# Revit family: Lighting-CommercialSector-GEWISS-ELIA-PL-LED_FLUSH_MOUNTING
name_source: partatom
category: Apparecchi per illuminazione
units: mm (PartAtom-declared; Revit-internal decimal feet)

## family parameters
Condiviso = No
Host = Superficie
Punto di calcolo locali = Sì
Quota connettore circolare = Usa diametro
Sorgente d'illuminazione = Sì
Taglio con vuoti quando caricato = No
Tipo di parte = Normale

## types (48) — shared parameters
Angolo inclinazione = -90.00°
Application = Indoor
BORDO = BORDO
Catalogue = LIGHTING
Catalogue Range = ELIA PL
Colour = White
Emetti da lunghezza linea = 610 mm
FORO_CONTROSOFFITTO = 80 mm  [stored 0.262467 ft]
File diagramma fotometrico = GWF1611NN940.IES
Filtro dei colori = 16777215
IDF = 6f387c7b-be92-4833-a933-611e67cbe188
IDT = 4c6a4f10-3f0b-4303-adcc-d543444cbb8d
IP degree = IP20 - IP40
Immagine tipo = ELIA_PL_q.jpg
Installation = Modular flush mounting
Insulation class = II
LED Life time (L80B50) = L80 B50 (Tq25°) = 50.000h
L_lampada = 1500 mm  [stored 4.92126 ft]
Lamp = LED
Larghezza lampada = 620 mm  [stored 2.03412 ft]
Lunghezza lampada = 620 mm  [stored 2.03412 ft]
Operating temperature: = -20° +45°
POSIZIONE = 80000
Produttore = GEWISS S.p.A.
Prospetto di default = 1219 mm
SCHERMO LED = SCHERMO LED
SEO = LED modular flush mounting
Shock resistance = IK03
System power = 33W
Technical sheet = https://www.gewiss.com
Type of lamp = LED
Type of light source = LED - Not replaceable
Typology = Modular flush mounting
URL = https://www.gewiss.com
Variazione temperatura colore lampada con luminosità attenuata = <Nessuno>
Version file RFA = 20.0
Voltage = 220-240 VÂ
Warranty = 5 years
Working temperature = -20° +45°
corpo centrale = corpo centrale

## per-type parameters (varying)
| type | Colour temperature | Colour temperature: | Descrizione | Dimensions (mm) | Lumen output (lm) | Modello | Optic | UGR: | Weight (kg) | Weight (kg): |
| GWF1610NA830 - ELIA PL M3 OPAL 30K ON/OFF CRI80 | 3000K | 3000K | ELIA PL M3 OPAL 30K ON/OFF CRI80 | 62x62 | 3700 | GWF1610NA830 | Diffusing opal | UGR<22 | 2,6 | 2,6 |
| GWF1611LN840 - ELIA PL M1 MICROP.40K DALI CRI80 | 4000K | 4000K | ELIA PL M1 MICROP.40K DALI CRI80 | 30x120 | 3600 | GWF1611LN840 | Microprismatic | UGR<19 | 2,4 | 2,4 |
| GWF1610NA930 - ELIA PL M3 OPAL 30K ON/OFF CRI90 | 3000K | 3000K | ELIA PL M3 OPAL 30K ON/OFF CRI90 | 62x62 | 3500 | GWF1610NA930 | Diffusing opal | UGR<22 | 2,6 | 2,6 |
| GWF1610NN930 - ELIA PL M3 MICROP.30K ON/OFF CRI90 | 3000K | 3000K | ELIA PL M3 MICROP.30K ON/OFF CRI90 | 62x62 | 3000 | GWF1610NN930 | Microprismatic | UGR<19 | 2,6 | 2,6 |
| GWF1611MN830 - ELIA PL M2 MICROP.30K DALI CRI80 | 3000K | 3000K | ELIA PL M2 MICROP.30K DALI CRI80 | 60x60 | 3300 | GWF1611MN830 | Microprismatic | UGR<19 | 2,4 | 2,4 |
| GWF1610MN830 - ELIA PL M2 MICROP.30K ON/OFF CRI80 | 3000K | 3000K | ELIA PL M2 MICROP.30K ON/OFF CRI80 | 60x60 | 3300 | GWF1610MN830 | Microprismatic | UGR<19 | 2,4 | 2,4 |
| GWF1610MN840 - ELIA PL M2 MICROP.40K ON/OFF CRI80 | 4000K | 4000K | ELIA PL M2 MICROP.40K ON/OFF CRI80 | 60x60 | 3600 | GWF1610MN840 | Microprismatic | UGR<19 | 2,4 | 2,4 |
| GWF1610LA940 - ELIA PL M1 OPAL 40K ON/OFF CRI90 | 4000K | 4000K | ELIA PL M1 OPAL 40K ON/OFF CRI90 | 30x120 | 3700 | GWF1610LA940 | Diffusing opal | UGR<22 | 2,4 | 2,4 |
| GWF1610NA840 - ELIA PL M3 OPAL 40K ON/OFF CRI80 | 4000K | 4000K | ELIA PL M3 OPAL 40K ON/OFF CRI80 | 62x62 | 3900 | GWF1610NA840 | Diffusing opal | UGR<22 | 2,6 | 2,6 |
| GWF1611LA940 - ELIA PL M1 OPAL 40K DALI CRI90 | 4000K | 4000K | ELIA PL M1 OPAL 40K DALI CRI90 | 30x120 | 3700 | GWF1611LA940 | Diffusing opal | UGR<22 | 2,4 | 2,4 |
| GWF1611MN840 - ELIA PL M2 MICROP.40K DALI CRI80 | 4000K | 4000K | ELIA PL M2 MICROP.40K DALI CRI80 | 60x60 | 3600 | GWF1611MN840 | Microprismatic | UGR<19 | 2,4 | 2,4 |
| GWF1610LA930 - ELIA PL M1 OPAL 30K ON/OFF CRI90 | 3000K | 3000K | ELIA PL M1 OPAL 30K ON/OFF CRI90 | 30x120 | 3500 | GWF1610LA930 | Diffusing opal | UGR<22 | 2,4 | 2,4 |
| GWF1610NA940 - ELIA PL M3 OPAL 40K ON/OFF CRI90 | 4000K | 4000K | ELIA PL M3 OPAL 40K ON/OFF CRI90 | 62x62 | 3700 | GWF1610NA940 | Diffusing opal | UGR<22 | 2,6 | 2,6 |
| GWF1611LN940 - ELIA PL M1 MICROP.40K DALI CRI90 | 4000K | 4000K | ELIA PL M1 MICROP.40K DALI CRI90 | 30x120 | 3300 | GWF1611LN940 | Microprismatic | UGR<19 | 2,4 | 2,4 |
| GWF1610MA830 - ELIA PL M2 OPAL 30K ON/OFF CRI80 | 3000K | 3000K | ELIA PL M2 OPAL 30K ON/OFF CRI80 | 60x60 | 3700 | GWF1610MA830 | Diffusing opal | UGR<22 | 2,4 | 2,4 |
| GWF1610LA840 - ELIA PL M1 OPAL 40K ON/OFF CRI80 | 4000K | 4000K | ELIA PL M1 OPAL 40K ON/OFF CRI80 | 30x120 | 3900 | GWF1610LA840 | Diffusing opal | UGR<22 | 2,4 | 2,4 |
| GWF1611NA940 - ELIA PL M3 OPAL 40K DALI CRI90 | 4000K | 4000K | ELIA PL M3 OPAL 40K DALI CRI90 | 62x62 | 3700 | GWF1611NA940 | Diffusing opal | UGR<22 | 2,6 | 2,6 |
| GWF1611LA930 - ELIA PL M1 OPAL 30K DALI CRI90 | 3000K | 3000K | ELIA PL M1 OPAL 30K DALI CRI90 | 30x120 | 3500 | GWF1611LA930 | Diffusing opal | UGR<22 | 2,4 | 2,4 |
| GWF1610LN930 - ELIA PL M1 MICROP.30K ON/OFF CRI90 | 3000K | 3000K | ELIA PL M1 MICROP.30K ON/OFF CRI90 | 30x120 | 3000 | GWF1610LN930 | Microprismatic | UGR<19 | 2,4 | 2,4 |
| GWF1611NA840 - ELIA PL M3 OPAL 40K DALI CRI80 | 4000K | 4000K | ELIA PL M3 OPAL 40K DALI CRI80 | 62x62 | 3900 | GWF1611NA840 | Diffusing opal | UGR<22 | 2,6 | 2,6 |
| GWF1610LN830 - ELIA PL M1 MICROP.30K ON/OFF CRI80 | 3000K | 3000K | ELIA PL M1 MICROP.30K ON/OFF CRI80 | 30x120 | 3300 | GWF1610LN830 | Microprismatic | UGR<19 | 2,4 | 2,4 |
| GWF1610LN840 - ELIA PL M1 MICROP.40K ON/OFF CRI80 | 4000K | 4000K | ELIA PL M1 MICROP.40K ON/OFF CRI80 | 30x120 | 3600 | GWF1610LN840 | Microprismatic | UGR<19 | 2,4 | 2,4 |
| GWF1610LN940 - ELIA PL M1 MICROP.40K ON/OFF CRI90 | 4000K | 4000K | ELIA PL M1 MICROP.40K ON/OFF CRI90 | 30x120 | 3300 | GWF1610LN940 | Microprismatic | UGR<19 | 2,4 | 2,4 |
| GWF1611MN940 - ELIA PL M2 MICROP.40K DALI CRI90 | 4000K | 4000K | ELIA PL M2 MICROP.40K DALI CRI90 | 60x60 | 3300 | GWF1611MN940 | Microprismatic | UGR<19 | 2,4 | 2,4 |
| GWF1611MA930 - ELIA PL M2 OPAL 30K DALI CRI90 | 3000K | 3000K | ELIA PL M2 OPAL 30K DALI CRI90 | 60x60 | 3500 | GWF1611MA930 | Diffusing opal | UGR<22 | 2,4 | 2,4 |
| GWF1611LN830 - ELIA PL M1 MICROP.30K DALI CRI80 | 3000K | 3000K | ELIA PL M1 MICROP.30K DALI CRI80 | 30x120 | 3300 | GWF1611LN830 | Microprismatic | UGR<19 | 2,4 | 2,4 |
| GWF1611NN830 - ELIA PL M3 MICROP.30K DALI CRI80 | 3000K | 3000K | ELIA PL M3 MICROP.30K DALI CRI80 | 62x62 | 3300 | GWF1611NN830 | Microprismatic | UGR<19 | 2,6 | 2,6 |
| GWF1611NN940 - ELIA PL M3 MICROP.40K DALI CRI90 | 4000K | 4000K | ELIA PL M3 MICROP.40K DALI CRI90 | 62x62 | 3300 | GWF1611NN940 | Microprismatic | UGR<19 | 2,6 | 2,6 |
| GWF1611LA840 - ELIA PL M1 OPAL 40K DALI CRI80 | 4000K | 4000K | ELIA PL M1 OPAL 40K DALI CRI80 | 30x120 | 3900 | GWF1611LA840 | Diffusing opal | UGR<22 | 2,4 | 2,4 |
| GWF1610LA830 - ELIA PL M1 OPAL 30K ON/OFF CRI80 | 3000K | 3000K | ELIA PL M1 OPAL 30K ON/OFF CRI80 | 30x120 | 3700 | GWF1610LA830 | Diffusing opal | UGR<22 | 2,4 | 2,4 |
| GWF1611MA830 - ELIA PL M2 OPAL 30K DALI CRI80 | 3000K | 3000K | ELIA PL M2 OPAL 30K DALI CRI80 | 60x60 | 3700 | GWF1611MA830 | Diffusing opal | UGR<22 | 2,4 | 2,4 |
| GWF1611NN840 - ELIA PL M3 MICROP.40K DALI CRI80 | 4000K | 4000K | ELIA PL M3 MICROP.40K DALI CRI80 | 62x62 | 3600 | GWF1611NN840 | Microprismatic | UGR<19 | 2,6 | 2,6 |
| GWF1611MA940 - ELIA PL M2 OPAL 40K DALI CRI90 | 4000K | 4000K | ELIA PL M2 OPAL 40K DALI CRI90 | 60x60 | 3700 | GWF1611MA940 | Diffusing opal | UGR<22 | 2,4 | 2,4 |
| GWF1611NA830 - ELIA PL M3 OPAL 30K DALI CRI80 | 3000K | 3000K | ELIA PL M3 OPAL 30K DALI CRI80 | 62x62 | 3700 | GWF1611NA830 | Diffusing opal | UGR<22 | 2,6 | 2,6 |
| GWF1611NN930 - ELIA PL M3 MICROP.30K DALI CRI90 | 3000K | 3000K | ELIA PL M3 MICROP.30K DALI CRI90 | 62x62 | 3000 | GWF1611NN930 | Microprismatic | UGR<19 | 2,6 | 2,6 |
| GWF1610MA840 - ELIA PL M2 OPAL 40K ON/OFF CRI80 | 4000K | 4000K | ELIA PL M2 OPAL 40K ON/OFF CRI80 | 60x60 | 3900 | GWF1610MA840 | Diffusing opal | UGR<22 | 2,4 | 2,4 |
| GWF1611LA830 - ELIA PL M1 OPAL 30K DALI CRI80 | 3000K | 3000K | ELIA PL M1 OPAL 30K DALI CRI80 | 30x120 | 3700 | GWF1611LA830 | Diffusing opal | UGR<22 | 2,4 | 2,4 |
| GWF1611LN930 - ELIA PL M1 MICROP.30K DALI CRI90 | 3000K | 3000K | ELIA PL M1 MICROP.30K DALI CRI90 | 30x120 | 3000 | GWF1611LN930 | Microprismatic | UGR<19 | 2,4 | 2,4 |
| GWF1610NN940 - ELIA PL M3 MICROP.40K ON/OFF CRI90 | 4000K | 4000K | ELIA PL M3 MICROP.40K ON/OFF CRI90 | 62x62 | 3300 | GWF1610NN940 | Microprismatic | UGR<19 | 2,6 | 2,6 |
| GWF1610NN840 - ELIA PL M3 MICROP.40K ON/OFF CRI80 | 4000K | 4000K | ELIA PL M3 MICROP.40K ON/OFF CRI80 | 62x62 | 3600 | GWF1610NN840 | Microprismatic | UGR<19 | 2,6 | 2,6 |
| GWF1610MA930 - ELIA PL M2 OPAL 30K ON/OFF CRI90 | 3000K | 3000K | ELIA PL M2 OPAL 30K ON/OFF CRI90 | 60x60 | 3500 | GWF1610MA930 | Diffusing opal | UGR<22 | 2,4 | 2,4 |
| GWF1611NA930 - ELIA PL M3 OPAL 30K DALI CRI90 | 3000K | 3000K | ELIA PL M3 OPAL 30K DALI CRI90 | 62x62 | 3500 | GWF1611NA930 | Diffusing opal | UGR<22 | 2,6 | 2,6 |
| GWF1610NN830 - ELIA PL M3 MICROP.30K ON/OFF CRI80 | 3000K | 3000K | ELIA PL M3 MICROP.30K ON/OFF CRI80 | 62x62 | 3300 | GWF1610NN830 | Microprismatic | UGR<19 | 2,6 | 2,6 |
| GWF1611MN930 - ELIA PL M2 MICROP.30K DALI CRI90 | 3000K | 3000K | ELIA PL M2 MICROP.30K DALI CRI90 | 60x60 | 3000 | GWF1611MN930 | Microprismatic | UGR<19 | 2,4 | 2,4 |
| GWF1610MN930 - ELIA PL M2 MICROP.30K ON/OFF CRI90 | 3000K | 3000K | ELIA PL M2 MICROP.30K ON/OFF CRI90 | 60x60 | 3000 | GWF1610MN930 | Microprismatic | UGR<19 | 2,4 | 2,4 |
| GWF1610MA940 - ELIA PL M2 OPAL 40K ON/OFF CRI90 | 4000K | 4000K | ELIA PL M2 OPAL 40K ON/OFF CRI90 | 60x60 | 3700 | GWF1610MA940 | Diffusing opal | UGR<22 | 2,4 | 2,4 |
| GWF1610MN940 - ELIA PL M2 MICROP.40K ON/OFF CRI90 | 4000K | 4000K | ELIA PL M2 MICROP.40K ON/OFF CRI90 | 60x60 | 3300 | GWF1610MN940 | Microprismatic | UGR<19 | 2,4 | 2,4 |
| GWF1611MA840 - ELIA PL M2 OPAL 40K DALI CRI80 | 4000K | 4000K | ELIA PL M2 OPAL 40K DALI CRI80 | 60x60 | 3900 | GWF1611MA840 | Diffusing opal | UGR<22 | 2,4 | 2,4 |

note: [stored X ft] marks values corroborated as IEEE doubles in the binary element streams (Revit-internal decimal feet)
